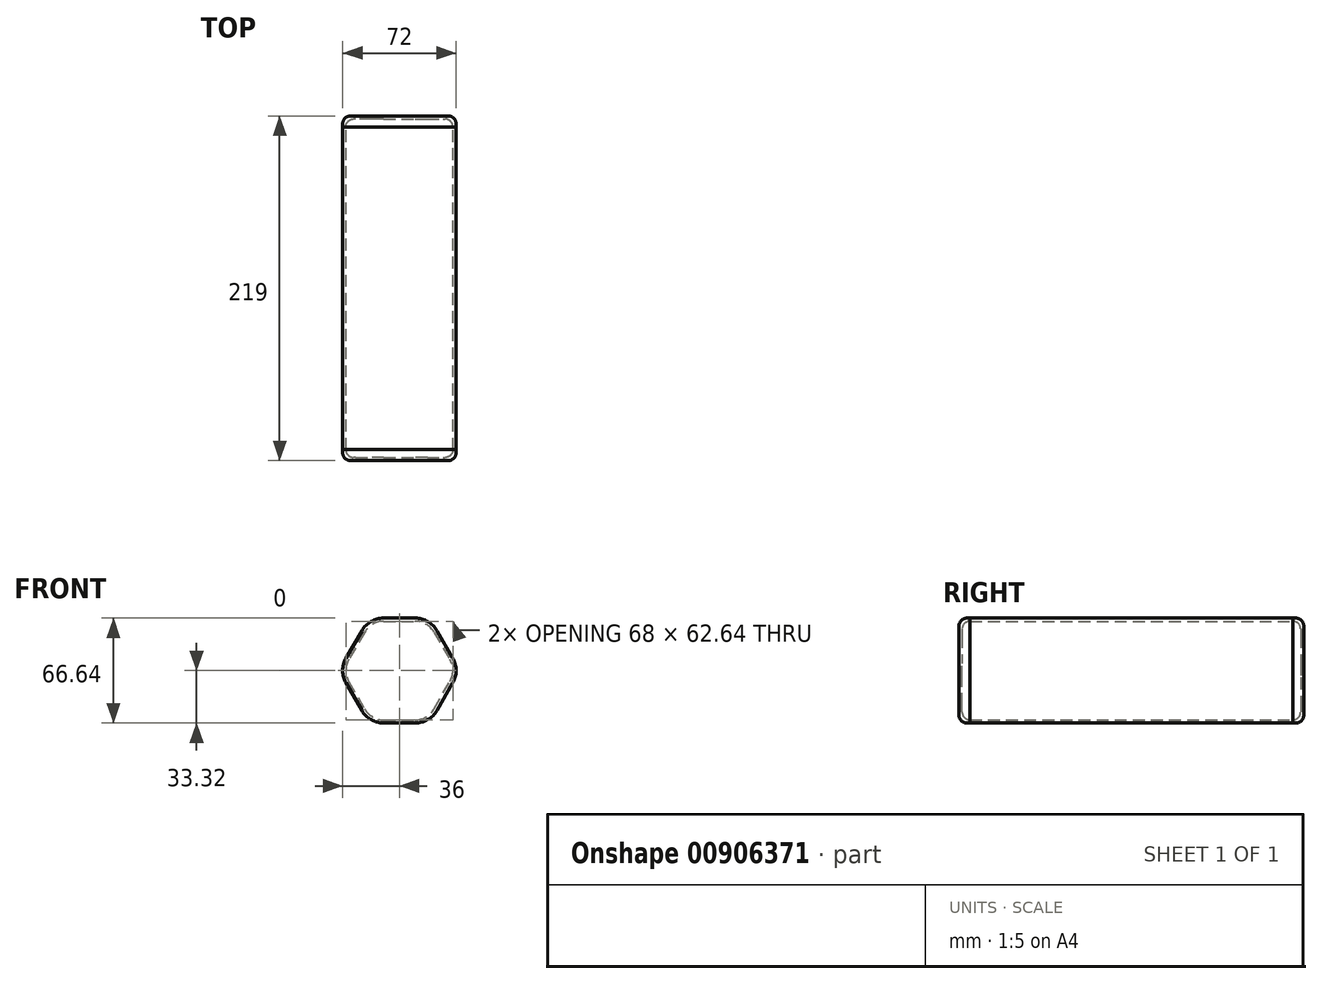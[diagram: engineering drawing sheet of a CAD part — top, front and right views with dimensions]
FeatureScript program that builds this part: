
annotation { "Feature Type Name" : "Feature", "Feature Type Description" : "" }
export const myFeature = defineFeature(function(context is Context, id is Id, definition is map)
    precondition{}
    {
        {
            var Q0;
            Q0=qCreatedBy(makeId("Front.planeOp"),FACE);
            var sketch = newSketch(context, id + "F0", { "sketchPlane" : qUnion([Q0])});
            skCircle(sketch, "E0", {"center": v(0, 0) * mm, "radius": 9 * mm});
            skCircle(sketch, "E1.1.0.0", {"center": v(20, 0) * mm, "radius": 9 * mm});
            skCircle(sketch, "E1.2.0.0", {"center": v(40, 0) * mm, "radius": 9 * mm});
            skLineSegment(sketch, "E1.direction1", {"start": v(0, 0) * mm, "end": v(20, 0) * mm, "construction": true});
            skCircle(sketch, "E2", {"center": v(10, 17.32) * mm, "radius": 9 * mm});
            skCircle(sketch, "E3", {"center": v(10, -17.32) * mm, "radius": 9 * mm});
            skCircle(sketch, "E4.1.0.0", {"center": v(30, 17.32) * mm, "radius": 9 * mm});
            skLineSegment(sketch, "E4.direction1", {"start": v(10, 17.32) * mm, "end": v(30, 17.32) * mm, "construction": true});
            skCircle(sketch, "E5.1.0.0", {"center": v(30, -17.32) * mm, "radius": 9 * mm});
            skLineSegment(sketch, "E5.direction1", {"start": v(10, -17.32) * mm, "end": v(30, -17.32) * mm, "construction": true});
            skSolve(sketch);
        }
        {
            var Q0;
            Q0=qCreatedBy(makeId("Front.planeOp"),FACE);
            var sketch = newSketch(context, id + "F1", { "sketchPlane" : qUnion([Q0])});
            skArc(sketch, "E6.0", {"start": v(10, 26.32) * mm, "mid": v(5.5, 25.11) * mm, "end": v(2.2, 21.82) * mm});
            skArc(sketch, "E7.0", {"start": v(37.8, 21.82) * mm, "mid": v(34.5, 25.11) * mm, "end": v(30, 26.32) * mm});
            skArc(sketch, "E8.0", {"start": v(30, -26.32) * mm, "mid": v(34.5, -25.11) * mm, "end": v(37.8, -21.82) * mm});
            skArc(sketch, "E9.0", {"start": v(2.2, -21.82) * mm, "mid": v(5.5, -25.11) * mm, "end": v(10, -26.32) * mm});
            skArc(sketch, "E10.0", {"start": v(-7.8, 4.5) * mm, "mid": v(-9, 0) * mm, "end": v(-7.8, -4.5) * mm});
            skArc(sketch, "E11.0", {"start": v(47.8, -4.5) * mm, "mid": v(49, 0) * mm, "end": v(47.8, 4.5) * mm});
            skLineSegment(sketch, "E12", {"start": v(2.2, 21.82) * mm, "end": v(-7.8, 4.5) * mm});
            skLineSegment(sketch, "E13", {"start": v(-7.8, -4.5) * mm, "end": v(2.2, -21.82) * mm});
            skLineSegment(sketch, "E14", {"start": v(10, -26.32) * mm, "end": v(30, -26.32) * mm});
            skLineSegment(sketch, "E15", {"start": v(10, 26.32) * mm, "end": v(30, 26.32) * mm});
            skLineSegment(sketch, "E16", {"start": v(37.8, 21.82) * mm, "end": v(47.8, 4.5) * mm});
            skLineSegment(sketch, "E17", {"start": v(37.8, -21.82) * mm, "end": v(47.8, -4.5) * mm});
            skLineSegment(sketch, "E18.0", {"start": v(10, 31.32) * mm, "end": v(30, 31.32) * mm});
            skArc(sketch, "E18.1", {"start": v(-2.12, -24.32) * mm, "mid": v(3, -29.44) * mm, "end": v(10, -31.32) * mm});
            skLineSegment(sketch, "E18.2", {"start": v(-12.12, -7) * mm, "end": v(-2.12, -24.32) * mm});
            skArc(sketch, "E18.3", {"start": v(-12.12, 7) * mm, "mid": v(-14, 0) * mm, "end": v(-12.12, -7) * mm});
            skLineSegment(sketch, "E18.4", {"start": v(-2.12, 24.32) * mm, "end": v(-12.12, 7) * mm});
            skLineSegment(sketch, "E18.5", {"start": v(10, -31.32) * mm, "end": v(30, -31.32) * mm});
            skArc(sketch, "E18.6", {"start": v(10, 31.32) * mm, "mid": v(3, 29.44) * mm, "end": v(-2.12, 24.32) * mm});
            skArc(sketch, "E18.7", {"start": v(30, -31.32) * mm, "mid": v(37, -29.44) * mm, "end": v(42.12, -24.32) * mm});
            skLineSegment(sketch, "E18.8", {"start": v(42.12, -24.32) * mm, "end": v(52.12, -7) * mm});
            skArc(sketch, "E18.9", {"start": v(52.12, -7) * mm, "mid": v(54, 0) * mm, "end": v(52.12, 7) * mm});
            skLineSegment(sketch, "E18.10", {"start": v(42.12, 24.32) * mm, "end": v(52.12, 7) * mm});
            skArc(sketch, "E18.11", {"start": v(42.12, 24.32) * mm, "mid": v(37, 29.44) * mm, "end": v(30, 31.32) * mm});
            skLineSegment(sketch, "E19.0", {"start": v(10, 33.32) * mm, "end": v(30, 33.32) * mm});
            skArc(sketch, "E19.1", {"start": v(-3.86, -25.32) * mm, "mid": v(2, -31.18) * mm, "end": v(10, -33.32) * mm});
            skLineSegment(sketch, "E19.2", {"start": v(-13.86, -8) * mm, "end": v(-3.86, -25.32) * mm});
            skArc(sketch, "E19.3", {"start": v(-13.86, 8) * mm, "mid": v(-16, 0) * mm, "end": v(-13.86, -8) * mm});
            skLineSegment(sketch, "E19.4", {"start": v(-3.86, 25.32) * mm, "end": v(-13.86, 8) * mm});
            skLineSegment(sketch, "E19.5", {"start": v(10, -33.32) * mm, "end": v(30, -33.32) * mm});
            skArc(sketch, "E19.6", {"start": v(10, 33.32) * mm, "mid": v(2, 31.18) * mm, "end": v(-3.86, 25.32) * mm});
            skArc(sketch, "E19.7", {"start": v(30, -33.32) * mm, "mid": v(38, -31.18) * mm, "end": v(43.86, -25.32) * mm});
            skLineSegment(sketch, "E19.8", {"start": v(43.86, -25.32) * mm, "end": v(53.86, -8) * mm});
            skArc(sketch, "E19.9", {"start": v(53.86, -8) * mm, "mid": v(56, 0) * mm, "end": v(53.86, 8) * mm});
            skLineSegment(sketch, "E19.10", {"start": v(43.86, 25.32) * mm, "end": v(53.86, 8) * mm});
            skArc(sketch, "E19.11", {"start": v(43.86, 25.32) * mm, "mid": v(38, 31.18) * mm, "end": v(30, 33.32) * mm});
            skSolve(sketch);
        }
        {
            var Q0;
            Q0=makeQuery(id+"F1.imprint","IMPRINT",FACE,{"disambiguationData":[TD([[makeQuery(id+"F1.imprint","IMPRINT",EDGE,{"derivedFrom":sQuery(id+"F1.wireOp",EDGE,"E18.0")}),1.0]])]});
            extrude(context, id + "F2", {"entities" : qUnion([Q0]), "depth" : 205 * mm, "offsetDistance" : 25 * mm});
        }
        {
            var Q0;
            Q0=makeQuery(id+"F2.opExtrude","CAP_FACE",FACE,{"disambiguationData":[OSD([sQuery(id+"F1.wireOp",EDGE,"E18.0"),sQuery(id+"F1.wireOp",EDGE,"E18.1"),sQuery(id+"F1.wireOp",EDGE,"E18.2"),sQuery(id+"F1.wireOp",EDGE,"E18.3"),sQuery(id+"F1.wireOp",EDGE,"E18.4"),sQuery(id+"F1.wireOp",EDGE,"E18.5"),sQuery(id+"F1.wireOp",EDGE,"E18.6"),sQuery(id+"F1.wireOp",EDGE,"E18.7"),sQuery(id+"F1.wireOp",EDGE,"E18.8"),sQuery(id+"F1.wireOp",EDGE,"E18.9"),sQuery(id+"F1.wireOp",EDGE,"E18.10"),sQuery(id+"F1.wireOp",EDGE,"E18.11"),sQuery(id+"F1.wireOp",EDGE,"E19.0"),sQuery(id+"F1.wireOp",EDGE,"E19.1"),sQuery(id+"F1.wireOp",EDGE,"E19.2"),sQuery(id+"F1.wireOp",EDGE,"E19.3"),sQuery(id+"F1.wireOp",EDGE,"E19.4"),sQuery(id+"F1.wireOp",EDGE,"E19.5"),sQuery(id+"F1.wireOp",EDGE,"E19.6"),sQuery(id+"F1.wireOp",EDGE,"E19.7"),sQuery(id+"F1.wireOp",EDGE,"E19.8"),sQuery(id+"F1.wireOp",EDGE,"E19.9"),sQuery(id+"F1.wireOp",EDGE,"E19.10"),sQuery(id+"F1.wireOp",EDGE,"E19.11")])],"isStart":false});
            var sketch = newSketch(context, id + "F3", { "sketchPlane" : qUnion([Q0])});
            skLineSegment(sketch, "E20.0.0", {"start": v(10, -33.32) * mm, "end": v(30, -33.32) * mm});
            skArc(sketch, "E20.0.1", {"start": v(30, -33.32) * mm, "mid": v(38, -31.18) * mm, "end": v(43.86, -25.32) * mm});
            skLineSegment(sketch, "E20.0.2", {"start": v(43.86, -25.32) * mm, "end": v(53.86, -8) * mm});
            skArc(sketch, "E20.0.3", {"start": v(53.86, -8) * mm, "mid": v(56, 0) * mm, "end": v(53.86, 8) * mm});
            skLineSegment(sketch, "E20.0.4", {"start": v(53.86, 8) * mm, "end": v(43.86, 25.32) * mm});
            skArc(sketch, "E20.0.5", {"start": v(43.86, 25.32) * mm, "mid": v(38, 31.18) * mm, "end": v(30, 33.32) * mm});
            skLineSegment(sketch, "E20.0.6", {"start": v(30, 33.32) * mm, "end": v(10, 33.32) * mm});
            skArc(sketch, "E20.0.7", {"start": v(10, 33.32) * mm, "mid": v(2, 31.18) * mm, "end": v(-3.86, 25.32) * mm});
            skLineSegment(sketch, "E20.0.8", {"start": v(-3.86, 25.32) * mm, "end": v(-13.86, 8) * mm});
            skArc(sketch, "E20.0.9", {"start": v(-13.86, 8) * mm, "mid": v(-16, 0) * mm, "end": v(-13.86, -8) * mm});
            skLineSegment(sketch, "E20.0.10", {"start": v(-13.86, -8) * mm, "end": v(-3.86, -25.32) * mm});
            skArc(sketch, "E20.0.11", {"start": v(-3.86, -25.32) * mm, "mid": v(2, -31.18) * mm, "end": v(10, -33.32) * mm});
            skArc(sketch, "E21.0", {"start": v(10, 31.32) * mm, "mid": v(3, 29.44) * mm, "end": v(-2.12, 24.32) * mm});
            skLineSegment(sketch, "E22.0", {"start": v(-2.12, 24.32) * mm, "end": v(-12.12, 7) * mm});
            skArc(sketch, "E23.0", {"start": v(-12.12, 7) * mm, "mid": v(-14, 0) * mm, "end": v(-12.12, -7) * mm});
            skLineSegment(sketch, "E24.0", {"start": v(-12.12, -7) * mm, "end": v(-2.12, -24.32) * mm});
            skLineSegment(sketch, "E25.0", {"start": v(10, 31.32) * mm, "end": v(30, 31.32) * mm});
            skArc(sketch, "E26.0", {"start": v(42.12, 24.32) * mm, "mid": v(37, 29.44) * mm, "end": v(30, 31.32) * mm});
            skLineSegment(sketch, "E27.0", {"start": v(42.12, 24.32) * mm, "end": v(52.12, 7) * mm});
            skArc(sketch, "E28.0", {"start": v(52.12, -7) * mm, "mid": v(54, 0) * mm, "end": v(52.12, 7) * mm});
            skArc(sketch, "E29.0", {"start": v(-2.12, -24.32) * mm, "mid": v(3, -29.44) * mm, "end": v(10, -31.32) * mm});
            skLineSegment(sketch, "E30.0", {"start": v(10, -31.32) * mm, "end": v(30, -31.32) * mm});
            skArc(sketch, "E31.0", {"start": v(30, -31.32) * mm, "mid": v(37, -29.44) * mm, "end": v(42.12, -24.32) * mm});
            skLineSegment(sketch, "E32.0", {"start": v(42.12, -24.32) * mm, "end": v(52.12, -7) * mm});
            skSolve(sketch);
        }
        {
            var Q0;
            Q0 = qSketchRegion(id + "F3", true);
            extrude(context, id + "F4", {"entities" : qUnion([Q0]), "depth" : 5 * mm, "offsetDistance" : 25 * mm});
        }
        {
            var Q0;
            Q0=makeQuery(id+"F4.opExtrude","CAP_FACE",FACE,{"disambiguationData":[OSD([sQuery(id+"F3.wireOp",EDGE,"E20.0.0"),sQuery(id+"F3.wireOp",EDGE,"E20.0.1"),sQuery(id+"F3.wireOp",EDGE,"E20.0.2"),sQuery(id+"F3.wireOp",EDGE,"E20.0.3"),sQuery(id+"F3.wireOp",EDGE,"E20.0.4"),sQuery(id+"F3.wireOp",EDGE,"E20.0.5"),sQuery(id+"F3.wireOp",EDGE,"E20.0.6"),sQuery(id+"F3.wireOp",EDGE,"E20.0.7"),sQuery(id+"F3.wireOp",EDGE,"E20.0.8"),sQuery(id+"F3.wireOp",EDGE,"E20.0.9"),sQuery(id+"F3.wireOp",EDGE,"E20.0.10"),sQuery(id+"F3.wireOp",EDGE,"E20.0.11"),sQuery(id+"F3.wireOp",EDGE,"E21.0"),sQuery(id+"F3.wireOp",EDGE,"E22.0"),sQuery(id+"F3.wireOp",EDGE,"E23.0"),sQuery(id+"F3.wireOp",EDGE,"E24.0"),sQuery(id+"F3.wireOp",EDGE,"E25.0"),sQuery(id+"F3.wireOp",EDGE,"E26.0"),sQuery(id+"F3.wireOp",EDGE,"E27.0"),sQuery(id+"F3.wireOp",EDGE,"E28.0"),sQuery(id+"F3.wireOp",EDGE,"E29.0"),sQuery(id+"F3.wireOp",EDGE,"E30.0"),sQuery(id+"F3.wireOp",EDGE,"E31.0"),sQuery(id+"F3.wireOp",EDGE,"E32.0")])],"isStart":false});
            var sketch = newSketch(context, id + "F5", { "sketchPlane" : qUnion([Q0])});
            skArc(sketch, "E33.0.0", {"start": v(-3.86, -25.32) * mm, "mid": v(2, -31.18) * mm, "end": v(10, -33.32) * mm});
            skLineSegment(sketch, "E33.0.1", {"start": v(10, -33.32) * mm, "end": v(30, -33.32) * mm});
            skArc(sketch, "E33.0.2", {"start": v(30, -33.32) * mm, "mid": v(38, -31.18) * mm, "end": v(43.86, -25.32) * mm});
            skLineSegment(sketch, "E33.0.3", {"start": v(43.86, -25.32) * mm, "end": v(53.86, -8) * mm});
            skArc(sketch, "E33.0.4", {"start": v(53.86, -8) * mm, "mid": v(56, 0) * mm, "end": v(53.86, 8) * mm});
            skLineSegment(sketch, "E33.0.5", {"start": v(53.86, 8) * mm, "end": v(43.86, 25.32) * mm});
            skArc(sketch, "E33.0.6", {"start": v(43.86, 25.32) * mm, "mid": v(38, 31.18) * mm, "end": v(30, 33.32) * mm});
            skLineSegment(sketch, "E33.0.7", {"start": v(30, 33.32) * mm, "end": v(10, 33.32) * mm});
            skArc(sketch, "E33.0.8", {"start": v(10, 33.32) * mm, "mid": v(2, 31.18) * mm, "end": v(-3.86, 25.32) * mm});
            skLineSegment(sketch, "E33.0.9", {"start": v(-3.86, 25.32) * mm, "end": v(-13.86, 8) * mm});
            skArc(sketch, "E33.0.10", {"start": v(-13.86, 8) * mm, "mid": v(-16, 0) * mm, "end": v(-13.86, -8) * mm});
            skLineSegment(sketch, "E33.0.11", {"start": v(-13.86, -8) * mm, "end": v(-3.86, -25.32) * mm});
            skSolve(sketch);
        }
        {
            var Q0;
            Q0=makeQuery(id+"F5.imprint","IMPRINT",FACE,{"disambiguationData":[TD([[makeQuery(id+"F5.imprint","IMPRINT",EDGE,{"derivedFrom":makeQuery(id+"F4.opExtrude","CAP_EDGE",EDGE,{"disambiguationData":[OSD([sQuery(id+"F3.wireOp",EDGE,"E21.0")])],"isStart":false})}),1.0]])]});
            var Q1;
            Q1=makeQuery(id+"F5.imprint","IMPRINT",FACE,{"disambiguationData":[TD([[makeQuery(id+"F5.imprint","IMPRINT",EDGE,{"derivedFrom":sQuery(id+"F5.wireOp",EDGE,"E33.0.0")}),1.0]])]});
            extrude(context, id + "F6", {"entities" : qUnion([Q0, Q1]), "operationType" : NewBodyOperationType.ADD, "depth" : 2 * mm, "offsetDistance" : 25 * mm});
        }
        {
            var Q0;
            Q0=makeQuery(id+"F6.opExtrude","CAP_FACE",FACE,{"disambiguationData":[OSD([sQuery(id+"F5.wireOp",EDGE,"E33.0.0"),sQuery(id+"F5.wireOp",EDGE,"E33.0.1"),sQuery(id+"F5.wireOp",EDGE,"E33.0.2"),sQuery(id+"F5.wireOp",EDGE,"E33.0.3"),sQuery(id+"F5.wireOp",EDGE,"E33.0.4"),sQuery(id+"F5.wireOp",EDGE,"E33.0.5"),sQuery(id+"F5.wireOp",EDGE,"E33.0.6"),sQuery(id+"F5.wireOp",EDGE,"E33.0.7"),sQuery(id+"F5.wireOp",EDGE,"E33.0.8"),sQuery(id+"F5.wireOp",EDGE,"E33.0.9"),sQuery(id+"F5.wireOp",EDGE,"E33.0.10"),sQuery(id+"F5.wireOp",EDGE,"E33.0.11")])],"isStart":false});
            fillet(context, id + "F7", {"entities" : qUnion([Q0]), "radius" : 5 * mm, "tangentPropagation" : true, "allowEdgeOverflow" : false});
        }
        {
            var Q0;
            Q0=makeQuery(id+"F6.opExtrude","CAP_FACE",FACE,{"disambiguationData":[OSD([sQuery(id+"F5.wireOp",EDGE,"E33.0.0"),sQuery(id+"F5.wireOp",EDGE,"E33.0.1"),sQuery(id+"F5.wireOp",EDGE,"E33.0.2"),sQuery(id+"F5.wireOp",EDGE,"E33.0.3"),sQuery(id+"F5.wireOp",EDGE,"E33.0.4"),sQuery(id+"F5.wireOp",EDGE,"E33.0.5"),sQuery(id+"F5.wireOp",EDGE,"E33.0.6"),sQuery(id+"F5.wireOp",EDGE,"E33.0.7"),sQuery(id+"F5.wireOp",EDGE,"E33.0.8"),sQuery(id+"F5.wireOp",EDGE,"E33.0.9"),sQuery(id+"F5.wireOp",EDGE,"E33.0.10"),sQuery(id+"F5.wireOp",EDGE,"E33.0.11")])],"isStart":true});
            fillet(context, id + "F8", {"entities" : qUnion([Q0]), "radius" : 5 * mm, "tangentPropagation" : true, "allowEdgeOverflow" : false});
        }
        {
            var Q0;
            Q0=qCreatedBy(makeId("Front.planeOp"),FACE);
            cPlane(context, id + "F9", {"entities" : qUnion([Q0]), "cplaneType" : CPlaneType.OFFSET, "offset" : 102.5 * mm, "width" : 150 * mm, "height" : 150 * mm});
        }
        {
            var Q0;
            Q0=makeQuery(id+"F4.opExtrude","SWEPT_BODY",BODY,{"disambiguationData":[OSD([sQuery(id+"F3.wireOp",EDGE,"E20.0.0"),sQuery(id+"F3.wireOp",EDGE,"E20.0.1"),sQuery(id+"F3.wireOp",EDGE,"E20.0.2"),sQuery(id+"F3.wireOp",EDGE,"E20.0.3"),sQuery(id+"F3.wireOp",EDGE,"E20.0.4"),sQuery(id+"F3.wireOp",EDGE,"E20.0.5"),sQuery(id+"F3.wireOp",EDGE,"E20.0.6"),sQuery(id+"F3.wireOp",EDGE,"E20.0.7"),sQuery(id+"F3.wireOp",EDGE,"E20.0.8"),sQuery(id+"F3.wireOp",EDGE,"E20.0.9"),sQuery(id+"F3.wireOp",EDGE,"E20.0.10"),sQuery(id+"F3.wireOp",EDGE,"E20.0.11"),sQuery(id+"F3.wireOp",EDGE,"E21.0"),sQuery(id+"F3.wireOp",EDGE,"E22.0"),sQuery(id+"F3.wireOp",EDGE,"E23.0"),sQuery(id+"F3.wireOp",EDGE,"E24.0"),sQuery(id+"F3.wireOp",EDGE,"E25.0"),sQuery(id+"F3.wireOp",EDGE,"E26.0"),sQuery(id+"F3.wireOp",EDGE,"E27.0"),sQuery(id+"F3.wireOp",EDGE,"E28.0"),sQuery(id+"F3.wireOp",EDGE,"E29.0"),sQuery(id+"F3.wireOp",EDGE,"E30.0"),sQuery(id+"F3.wireOp",EDGE,"E31.0"),sQuery(id+"F3.wireOp",EDGE,"E32.0")])]});
            var Q1;
            Q1=qCreatedBy(id+"F9.planeOp",FACE);
            mirror(context, id + "F10", {"entities" : qUnion([Q0]), "mirrorPlane" : qUnion([Q1])});
        }
    });
